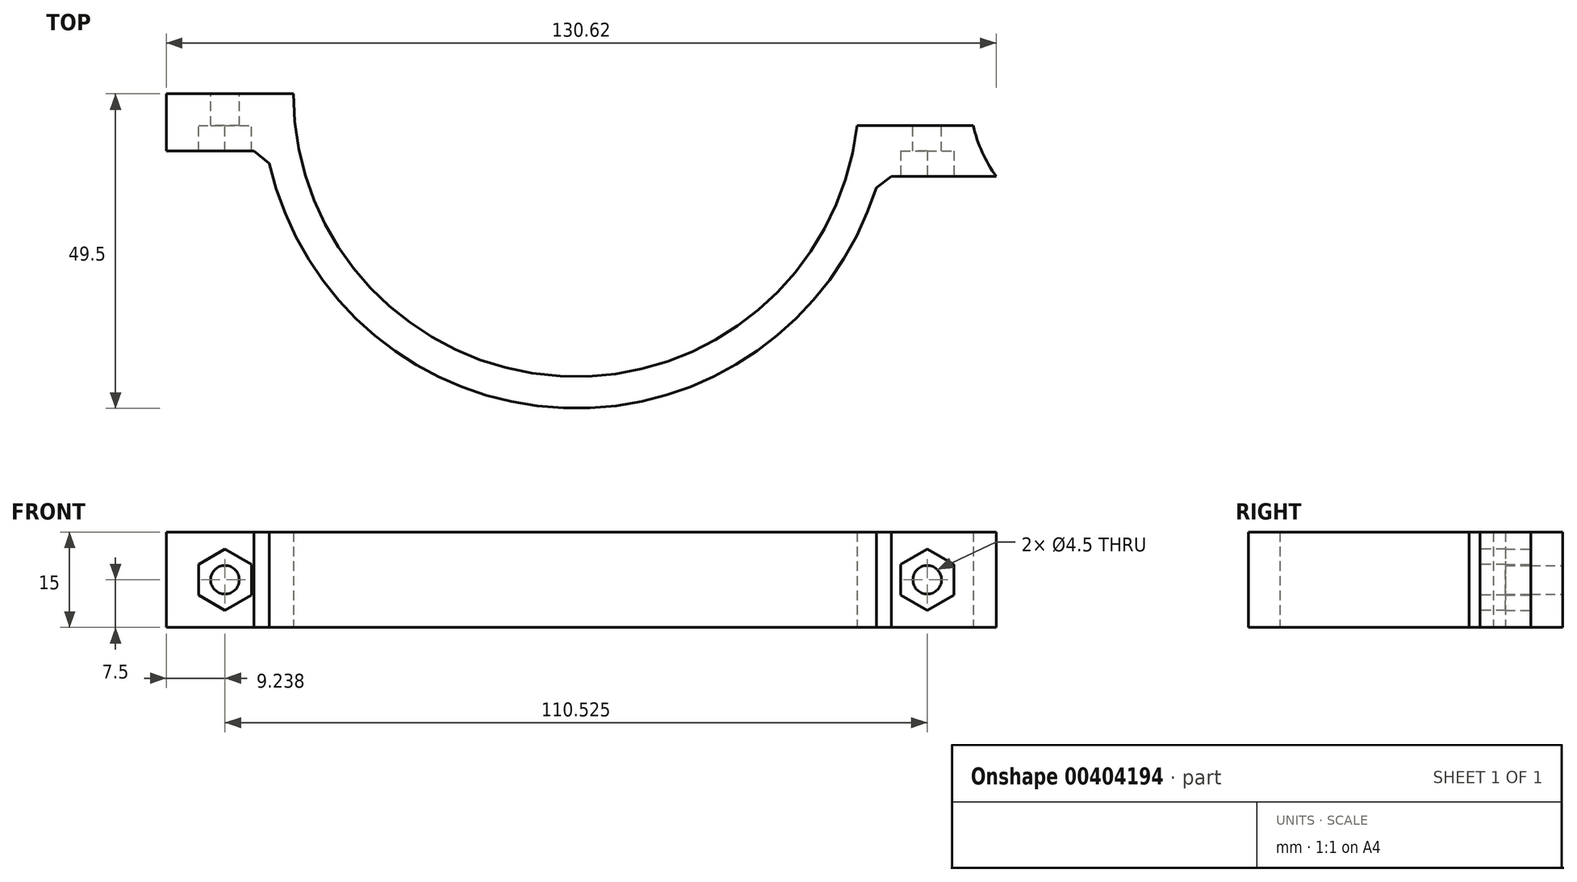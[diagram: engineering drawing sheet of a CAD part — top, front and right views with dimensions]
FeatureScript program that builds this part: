
annotation { "Feature Type Name" : "Feature", "Feature Type Description" : "" }
export const myFeature = defineFeature(function(context is Context, id is Id, definition is map)
    precondition{}
    {
        {
            var Q0;
            Q0=qCreatedBy(makeId("Top.planeOp"),FACE);
            var sketch = newSketch(context, id + "F0", { "sketchPlane" : qUnion([Q0])});
            skArc(sketch, "E0", {"start": v(44.5, 0) * mm, "mid": v(-44.43, 2.5) * mm, "end": v(44.22, -5) * mm, "construction": true});
            skArc(sketch, "E1", {"start": v(-44.5, 0) * mm, "mid": v(-2.5, -44.43) * mm, "end": v(44.22, -5) * mm});
            skLineSegment(sketch, "E2", {"start": v(-44.5, 0) * mm, "end": v(-64.5, 0) * mm});
            skLineSegment(sketch, "E3", {"start": v(-64.5, 0) * mm, "end": v(-64.5, -5) * mm});
            skLineSegment(sketch, "E4", {"start": v(-64.5, -5) * mm, "end": v(-49.25, -5) * mm});
            skArc(sketch, "E5", {"start": v(47.76, -13) * mm, "mid": v(-4.07, -49.33) * mm, "end": v(-49.25, -5) * mm});
            skLineSegment(sketch, "E6.MirrorCS", {"start": v(44.5, 0) * mm, "end": v(64.5, 0) * mm, "construction": true});
            skLineSegment(sketch, "E7", {"start": v(64.5, 0) * mm, "end": v(64.5, -5) * mm, "construction": true});
            skLineSegment(sketch, "E8", {"start": v(62.5, -5) * mm, "end": v(49.25, -5) * mm});
            skPoint(sketch, "E9.orphan", {"position": v(49.25, -5) * mm});
            skLineSegment(sketch, "E10", {"start": v(44.22, -5) * mm, "end": v(49.25, -5) * mm});
            skLineSegment(sketch, "E11", {"start": v(64.5, -5) * mm, "end": v(64.5, -13) * mm, "construction": true});
            skLineSegment(sketch, "E12", {"start": v(64.5, -13) * mm, "end": v(47.76, -13) * mm});
            skArc(sketch, "E13", {"start": v(67.67, -5) * mm, "mid": v(69.7, -9.36) * mm, "end": v(72.84, -13) * mm, "construction": true});
            skArc(sketch, "E14", {"start": v(62.5, -5) * mm, "mid": v(63.91, -9.18) * mm, "end": v(66.12, -13) * mm});
            skLineSegment(sketch, "E15", {"start": v(66.12, -13) * mm, "end": v(64.5, -13) * mm});
            skSolve(sketch);
        }
        {
            var Q0;
            Q0=qSketchRegion(id+"F0",true);
            extrude(context, id + "F1", {"entities" : qUnion([Q0]), "endBound" : BoundingType.SYMMETRIC, "depth" : 15 * mm});
        }
        {
            var Q0;
            Q0=makeQuery(id+"F1.opExtrude","SWEPT_FACE",FACE,{"disambiguationData":[OSD([sQuery(id+"F0.wireOp",EDGE,"E2")])]});
            var sketch = newSketch(context, id + "F2", { "sketchPlane" : qUnion([Q0])});
            skCircle(sketch, "E16", {"center": v(-55.26, 0) * mm, "radius": 2.25 * mm});
            skCircle(sketch, "E17.MirrorC", {"center": v(55.26, 0) * mm, "radius": 2.25 * mm});
            skSolve(sketch);
        }
        {
            var Q0;
            Q0=qSketchRegion(id+"F2",true);
            extrude(context, id + "F3", {"entities" : qUnion([Q0]), "operationType" : NewBodyOperationType.REMOVE, "oppositeDirection" : true, "depth" : 25 * mm});
        }
        {
            var Q0;
            Q0=makeQuery(id+"F1.opExtrude","SWEPT_FACE",FACE,{"disambiguationData":[OSD([sQuery(id+"F0.wireOp",EDGE,"E12")])]});
            var sketch = newSketch(context, id + "F4", { "sketchPlane" : qUnion([Q0])});
            skCircle(sketch, "E18.cCircle", {"center": v(55.26, 0) * mm, "radius": 4.17 * mm, "construction": true});
            skLineSegment(sketch, "E18.0", {"start": v(59.44, 2.41) * mm, "end": v(59.44, -2.41) * mm});
            skLineSegment(sketch, "E18.1", {"start": v(59.44, -2.41) * mm, "end": v(55.26, -4.82) * mm});
            skLineSegment(sketch, "E18.2", {"start": v(55.26, -4.82) * mm, "end": v(51.09, -2.41) * mm});
            skLineSegment(sketch, "E18.3", {"start": v(51.09, -2.41) * mm, "end": v(51.09, 2.41) * mm});
            skLineSegment(sketch, "E18.4", {"start": v(51.09, 2.41) * mm, "end": v(55.26, 4.82) * mm});
            skLineSegment(sketch, "E18.5", {"start": v(55.26, 4.82) * mm, "end": v(59.44, 2.41) * mm});
            skPoint(sketch, "E18.0.midPoint", {"position": v(59.44, 0) * mm});
            skSolve(sketch);
        }
        {
            var Q0;
            Q0=qSketchRegion(id+"F4",true);
            extrude(context, id + "F5", {"entities" : qUnion([Q0]), "operationType" : NewBodyOperationType.REMOVE, "oppositeDirection" : true, "depth" : 4 * mm});
        }
        {
            var Q0;
            Q0=makeQuery(id+"F1.opExtrude","SWEPT_FACE",FACE,{"disambiguationData":[OSD([sQuery(id+"F0.wireOp",EDGE,"E4")])]});
            var sketch = newSketch(context, id + "F6", { "sketchPlane" : qUnion([Q0])});
            skLineSegment(sketch, "E19.bottom", {"start": v(-64.5, 7.5) * mm, "end": v(-45.5, 7.5) * mm});
            skLineSegment(sketch, "E19.top", {"start": v(-64.5, -7.5) * mm, "end": v(-45.5, -7.5) * mm});
            skLineSegment(sketch, "E19.left", {"start": v(-64.5, 7.5) * mm, "end": v(-64.5, -7.5) * mm});
            skLineSegment(sketch, "E19.right", {"start": v(-45.5, 7.5) * mm, "end": v(-45.5, -7.5) * mm});
            skCircle(sketch, "E20.cCircle", {"center": v(-55.26, 0) * mm, "radius": 4.17 * mm, "construction": true});
            skLineSegment(sketch, "E20.0", {"start": v(-51.09, 2.41) * mm, "end": v(-51.09, -2.41) * mm});
            skLineSegment(sketch, "E20.1", {"start": v(-51.09, -2.41) * mm, "end": v(-55.26, -4.82) * mm});
            skLineSegment(sketch, "E20.2", {"start": v(-55.26, -4.82) * mm, "end": v(-59.44, -2.41) * mm});
            skLineSegment(sketch, "E20.3", {"start": v(-59.44, -2.41) * mm, "end": v(-59.44, 2.41) * mm});
            skLineSegment(sketch, "E20.4", {"start": v(-59.44, 2.41) * mm, "end": v(-55.26, 4.82) * mm});
            skLineSegment(sketch, "E20.5", {"start": v(-55.26, 4.82) * mm, "end": v(-51.09, 2.41) * mm});
            skPoint(sketch, "E20.0.midPoint", {"position": v(-51.09, 0) * mm});
            skSolve(sketch);
        }
        {
            var Q0;
            Q0 = qSketchRegion(id + "F6", true);
            extrude(context, id + "F7", {"entities" : qUnion([Q0]), "operationType" : NewBodyOperationType.ADD, "depth" : 4 * mm});
        }
        {
            var Q0;
            Q0=makeQuery(id+"F7.boolean.opBoolean","INTERSECT",EDGE,{"derivedFrom":[makeQuery(id+"F1.opExtrude","SWEPT_FACE",FACE,{"disambiguationData":[OSD([sQuery(id+"F0.wireOp",EDGE,"E5")])]}),makeQuery(id+"F7.opExtrude","CAP_FACE",FACE,{"disambiguationData":[OSD([sQuery(id+"F6.wireOp",EDGE,"E19.bottom"),sQuery(id+"F6.wireOp",EDGE,"E19.top"),sQuery(id+"F6.wireOp",EDGE,"E19.left"),sQuery(id+"F6.wireOp",EDGE,"E19.right"),sQuery(id+"F6.wireOp",EDGE,"E20.0"),sQuery(id+"F6.wireOp",EDGE,"E20.1"),sQuery(id+"F6.wireOp",EDGE,"E20.2"),sQuery(id+"F6.wireOp",EDGE,"E20.3"),sQuery(id+"F6.wireOp",EDGE,"E20.4"),sQuery(id+"F6.wireOp",EDGE,"E20.5")])],"isStart":false})]});
            var Q1;
            Q1=makeQuery(id+"F1.opExtrude","SWEPT_EDGE",EDGE,{"disambiguationData":[OSD([sQuery(id+"F0.wireOp",EDGE,"E5"),sQuery(id+"F0.wireOp",EDGE,"E12")])]});
            chamfer(context, id + "F8", {"entities" : qUnion([Q0, Q1]), "width" : 2.5 * mm, "tangentPropagation" : true});
        }
    });
